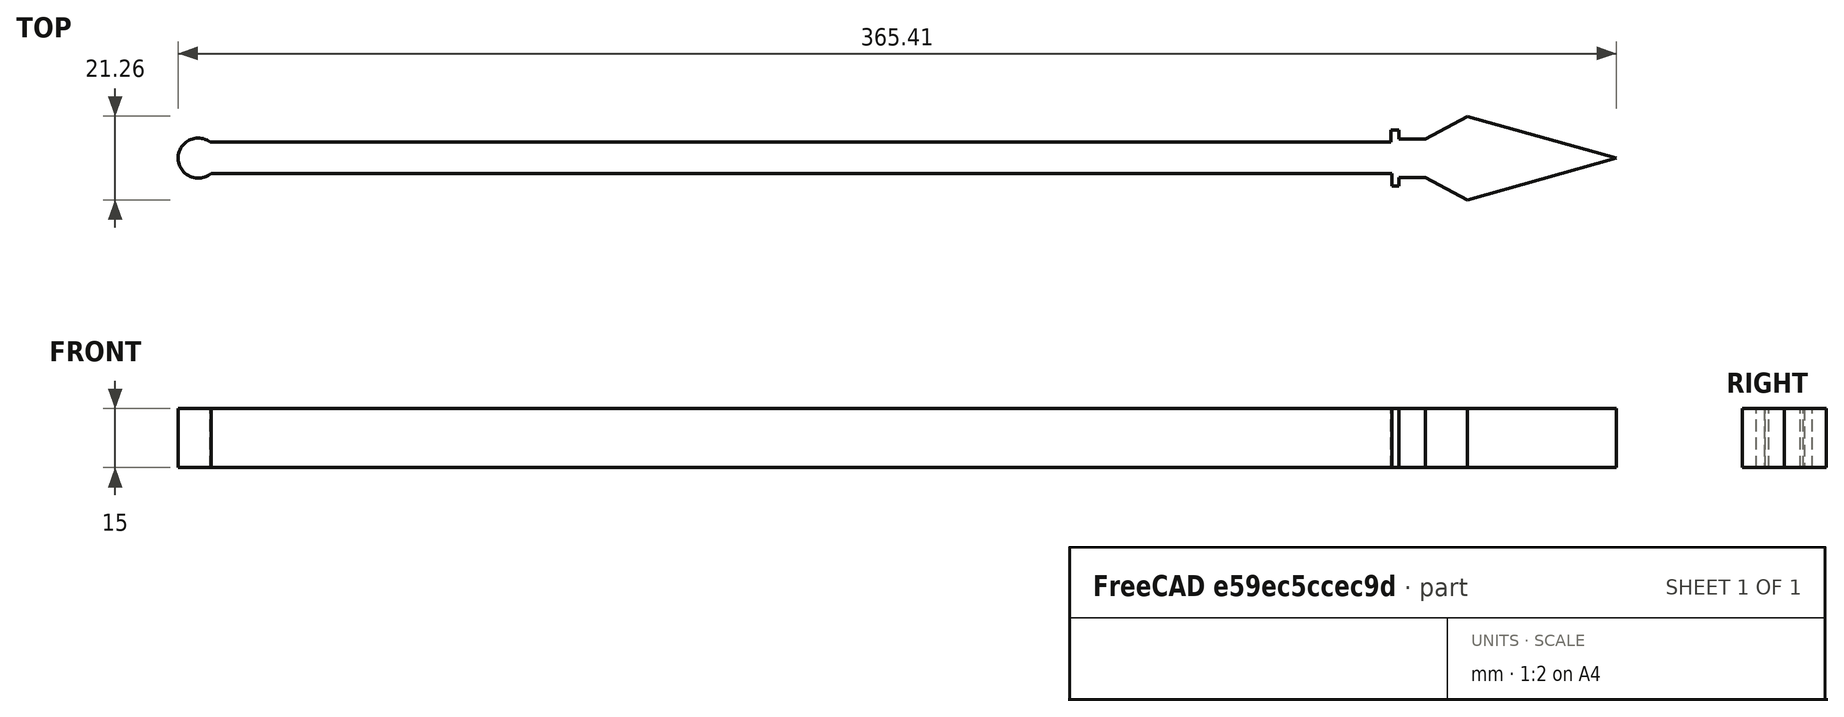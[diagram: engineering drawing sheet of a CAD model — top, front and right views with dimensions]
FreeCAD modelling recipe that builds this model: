
FCSTD DOCUMENT  (FreeCAD 0.16R6705 (Git))
Label: spada
License: All rights reserved
LicenseURL: http://it.wikipedia.org/wiki/<copyright redacted>
objects: Sketcher::SketchObject×3, PartDesign::Pad×1
note: 5 computed .brp shape members not serialized (recipe doc carries the construction recipe); baked Part::Feature solids carry a one-line shape summary decoded from their .brp

FEATURE [Sketcher::SketchObject] Sketch
  sketch-geometry (8):
    g0: LineSegment StartX=-203.39 StartY=-3.33346 StartZ=0 EndX=96.6096 EndY=-3.33346 EndZ=0
    g1: LineSegment StartX=96.6096 StartY=-9.48151 StartZ=0 EndX=96.6096 EndY=-3.33346 EndZ=0
    g2: LineSegment StartX=96.6096 StartY=-9.48151 StartZ=0 EndX=99.3052 EndY=-9.48151 EndZ=0
    g3: LineSegment StartX=99.3052 StartY=-9.48151 StartZ=0 EndX=99.3052 EndY=-4.9727 EndZ=0
    g4: LineSegment StartX=105.023 StartY=-4.9727 StartZ=0 EndX=116.029 EndY=-10.6279 EndZ=0
    g5: LineSegment StartX=116.029 StartY=-10.6279 StartZ=0 EndX=148 EndY=0 EndZ=0
    g6: LineSegment StartX=99.3052 StartY=-4.9727 StartZ=0 EndX=105.023 EndY=-4.9727 EndZ=0
    g7: ArcOfCircle CenterX=-207.759 CenterY=-2.48366 CenterZ=0 NormalX=0 NormalY=0 NormalZ=1 Radius=5.03095 StartAngle=2.62528 EndAngle=5.49677
  constraints (14):
    c: Coincident(g1,g0)
    c: Coincident(g2,g1)
    c: Vertical(g1)
    c: Coincident(g2,g3)
    c: Coincident(g5,g4)
    c: Coincident(g6,g4)
    c: Coincident(g3,g6)
    c: Vertical(g3)
    c: Horizontal(g6)
    c: PointOnObject(g5,g-1)
    c: Horizontal(g2)
    c: DistanceX(g0,g0) = 300
    c: Horizontal(g0)
    c: PointOnObject(g7,g-1)
FEATURE [Sketcher::SketchObject] MirroredSketch
  sketch-geometry (8):
    g0: LineSegment StartX=-203.39 StartY=3.33346 StartZ=0 EndX=96.6096 EndY=3.33346 EndZ=0
    g1: LineSegment StartX=96.6096 StartY=9.48151 StartZ=0 EndX=96.6096 EndY=3.33346 EndZ=0
    g2: LineSegment StartX=96.6096 StartY=9.48151 StartZ=0 EndX=99.3052 EndY=9.48151 EndZ=0
    g3: LineSegment StartX=99.3052 StartY=9.48151 StartZ=0 EndX=99.3052 EndY=4.9727 EndZ=0
    g4: LineSegment StartX=105.023 StartY=4.9727 StartZ=0 EndX=116.029 EndY=10.6279 EndZ=0
    g5: LineSegment StartX=116.029 StartY=10.6279 StartZ=0 EndX=148 EndY=0 EndZ=0
    g6: LineSegment StartX=99.3052 StartY=4.9727 StartZ=0 EndX=105.023 EndY=4.9727 EndZ=0
    g7: ArcOfCircle CenterX=-207.759 CenterY=2.48366 CenterZ=0 NormalX=0 NormalY=0 NormalZ=1 Radius=5.03095 StartAngle=0.786413 EndAngle=3.6579
  constraints (11):
    c: Coincident(g1,g0)
    c: Coincident(g2,g1)
    c: Vertical(g1)
    c: Coincident(g2,g3)
    c: Coincident(g5,g4)
    c: Coincident(g6,g4)
    c: Coincident(g3,g6)
    c: Vertical(g3)
    c: Horizontal(g6)
    c: Horizontal(g2)
    c: Horizontal(g0)
FEATURE [Sketcher::SketchObject] Sketch001
  sketch-geometry (15):
    g0: LineSegment StartX=-203.12 StartY=-3.8766 StartZ=0 EndX=96.8795 EndY=-3.8766 EndZ=0
    g1: LineSegment StartX=96.8795 StartY=-7.09161 StartZ=0 EndX=96.8795 EndY=-3.8766 EndZ=0
    g2: LineSegment StartX=96.8795 StartY=-7.09161 StartZ=0 EndX=98.6466 EndY=-7.09161 EndZ=0
    g3: LineSegment StartX=98.6466 StartY=-7.09161 StartZ=0 EndX=98.6466 EndY=-4.86457 EndZ=0
    g4: LineSegment StartX=105.328 StartY=-4.86457 StartZ=0 EndX=116.029 EndY=-10.6279 EndZ=0
    g5: LineSegment StartX=116.029 StartY=-10.6279 StartZ=0 EndX=153.887 EndY=0 EndZ=0
    g6: LineSegment StartX=98.6466 StartY=-4.86457 StartZ=0 EndX=105.328 EndY=-4.86457 EndZ=0
    g7: LineSegment StartX=-203.356 StartY=4.06582 StartZ=0 EndX=96.6096 EndY=4.06582 EndZ=0
    g8: LineSegment StartX=96.6096 StartY=7.09161 StartZ=0 EndX=96.6096 EndY=4.06582 EndZ=0
    g9: LineSegment StartX=96.6096 StartY=7.09161 StartZ=0 EndX=98.6466 EndY=7.09161 EndZ=0
    g10: LineSegment StartX=98.6466 StartY=7.09161 StartZ=0 EndX=98.6466 EndY=4.86457 EndZ=0
    g11: LineSegment StartX=105.328 StartY=4.86457 StartZ=0 EndX=116.029 EndY=10.6279 EndZ=0
    g12: LineSegment StartX=116.029 StartY=10.6279 StartZ=0 EndX=153.887 EndY=0 EndZ=0
    g13: LineSegment StartX=98.6466 StartY=4.86457 StartZ=0 EndX=105.328 EndY=4.86457 EndZ=0
    g14: ArcOfCircle CenterX=-206.425 CenterY=0 CenterZ=0 NormalX=0 NormalY=0 NormalZ=1 Radius=5.09368 StartAngle=0.924314 EndAngle=5.41824
  constraints (30):
    c: Coincident(g1,g0)
    c: Coincident(g2,g1)
    c: Vertical(g1)
    c: Coincident(g2,g3)
    c: Coincident(g5,g4)
    c: Coincident(g6,g4)
    c: Coincident(g3,g6)
    c: Vertical(g3)
    c: Horizontal(g6)
    c: PointOnObject(g5,g-1)
    c: Horizontal(g2)
    c: DistanceX(g0,g0) = 300
    c: Horizontal(g0)
    c: Coincident(g8,g7)
    c: Coincident(g9,g8)
    c: Vertical(g8)
    c: Coincident(g9,g10)
    c: Coincident(g12,g11)
    c: Coincident(g13,g11)
    c: Coincident(g10,g13)
    c: Vertical(g10)
    c: Horizontal(g13)
    c: Horizontal(g9)
    c: Horizontal(g7)
    c: Symmetric(g11,g4,g-1)
    c: Symmetric(g9,g2,g-1)
    c: Coincident(g12,g5)
    c: PointOnObject(g14,g-1)
    c: Coincident(g7,g14)
    c: Coincident(g0,g14)
FEATURE [PartDesign::Pad] Pad
  Length = 15
  Length2 = 100
  Sketch = -> Sketch001
  Type = 0
